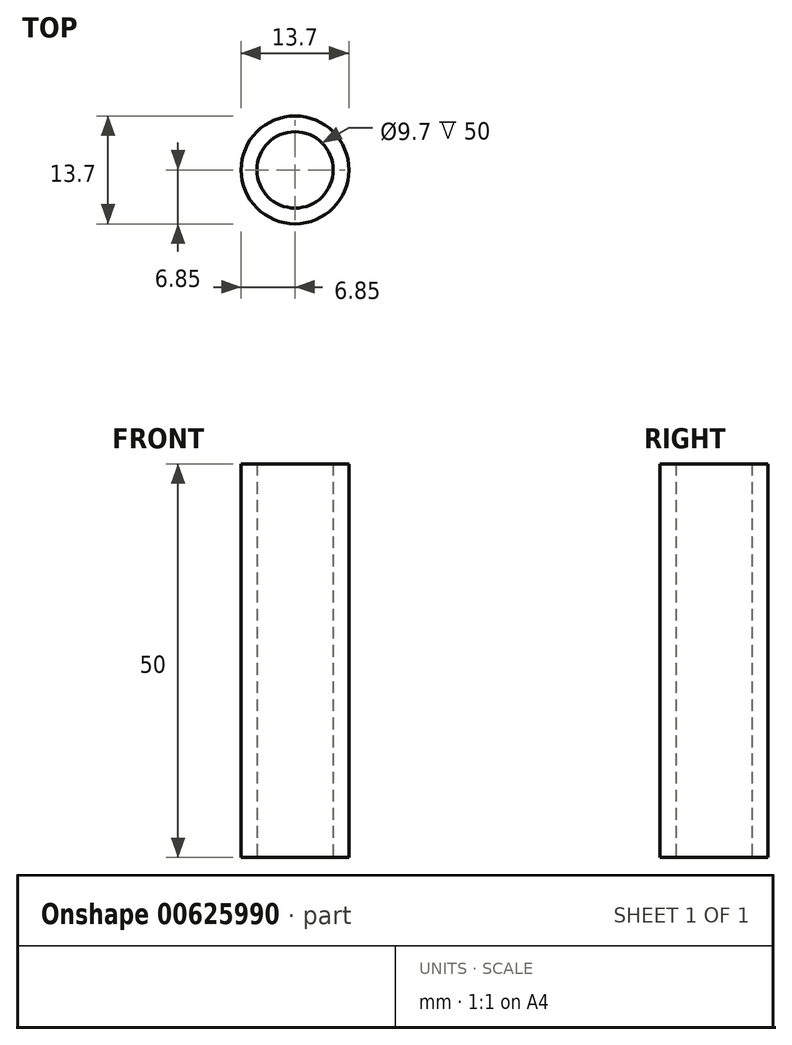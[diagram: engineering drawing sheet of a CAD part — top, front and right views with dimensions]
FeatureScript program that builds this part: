
annotation { "Feature Type Name" : "Feature", "Feature Type Description" : "" }
export const myFeature = defineFeature(function(context is Context, id is Id, definition is map)
    precondition{}
    {
        {
            var Q0;
            Q0=qCreatedBy(makeId("Top.planeOp"),FACE);
            var sketch = newSketch(context, id + "F0", { "sketchPlane" : qUnion([Q0])});
            skCircle(sketch, "E0", {"center": v(0, 0) * mm, "radius": 4.85 * mm});
            skCircle(sketch, "E1", {"center": v(0, 0) * mm, "radius": 6.85 * mm});
            skSolve(sketch);
        }
        {
            var Q0;
            Q0=makeQuery(id+"F0.imprint","IMPRINT",FACE,{"disambiguationData":[TD([[makeQuery(id+"F0.imprint","IMPRINT",EDGE,{"derivedFrom":sQuery(id+"F0.wireOp",EDGE,"E0")}),-1.0]])]});
            extrude(context, id + "F1", {"entities" : qUnion([Q0]), "depth" : 50 * mm, "offsetDistance" : 25 * mm});
        }
    });
